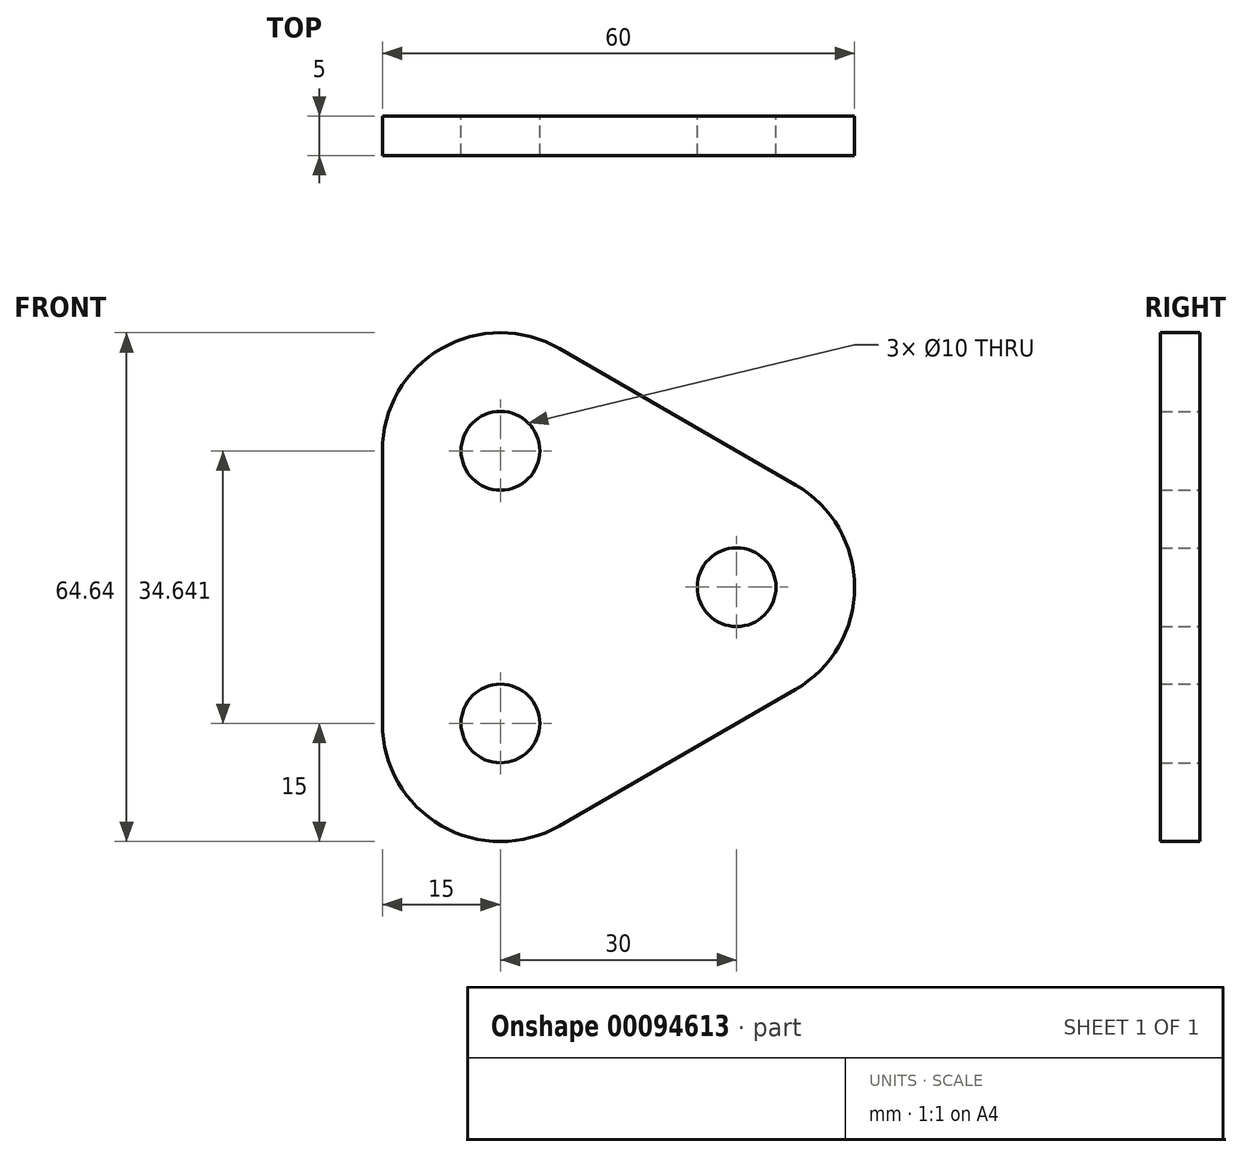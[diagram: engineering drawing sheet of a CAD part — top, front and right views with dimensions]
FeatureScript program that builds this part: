
annotation { "Feature Type Name" : "Feature", "Feature Type Description" : "" }
export const myFeature = defineFeature(function(context is Context, id is Id, definition is map)
    precondition{}
    {
        {
            var Q0;
            Q0=qCreatedBy(makeId("Front.planeOp"),FACE);
            var sketch = newSketch(context, id + "F0", { "sketchPlane" : qUnion([Q0])});
            skCircle(sketch, "E0", {"center": v(0, 0) * mm, "radius": 20 * mm, "construction": true});
            skLineSegment(sketch, "E1", {"start": v(0, 30.42) * mm, "end": v(0, -31.38) * mm, "construction": true});
            skLineSegment(sketch, "E2", {"start": v(-28.1, 0) * mm, "end": v(36.73, 0) * mm, "construction": true});
            skCircle(sketch, "E3", {"center": v(-10, 17.32) * mm, "radius": 5 * mm});
            skCircle(sketch, "E4.MirrorC", {"center": v(-10, -17.32) * mm, "radius": 5 * mm});
            skCircle(sketch, "E5", {"center": v(20, 0) * mm, "radius": 5 * mm});
            skLineSegment(sketch, "E6", {"start": v(-25, 17.32) * mm, "end": v(-25, -17.32) * mm});
            skLineSegment(sketch, "E7", {"start": v(-2.5, -30.31) * mm, "end": v(27.5, -13) * mm});
            skLineSegment(sketch, "E8", {"start": v(27.5, 13) * mm, "end": v(-2.5, 30.31) * mm});
            skArc(sketch, "E9.filletArc", {"start": v(-2.5, 30.31) * mm, "mid": v(-17.5, 30.31) * mm, "end": v(-25, 17.32) * mm});
            skPoint(sketch, "E10.visualSharp", {"position": v(-25, -43.3) * mm});
            skArc(sketch, "E10.filletArc", {"start": v(-25, -17.32) * mm, "mid": v(-17.5, -30.31) * mm, "end": v(-2.5, -30.31) * mm});
            skPoint(sketch, "E11.visualSharp", {"position": v(50, 0) * mm});
            skArc(sketch, "E11.filletArc", {"start": v(27.5, -13) * mm, "mid": v(35, 0) * mm, "end": v(27.5, 13) * mm});
            skSolve(sketch);
        }
        {
            var Q0;
            Q0 = qSketchRegion(id + "F0", true);
            extrude(context, id + "F1", {"entities" : qUnion([Q0]), "depth" : 5 * mm});
        }
    });
